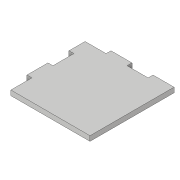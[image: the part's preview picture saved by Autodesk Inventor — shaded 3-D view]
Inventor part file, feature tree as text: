
AUTODESK INVENTOR PART (.ipt)
format: ipt  version: 2017 (Build 210142000, 142)  size: 99,840 bytes
history: native  units: in
note: dims shown in document units (in); Inventor stores cm internally (conversion verified against a paired STEP export)
features: extrude x2, sketch x2
ambient origin geometry x8: Origin, YZ Plane, XZ Plane, XY Plane, X Axis, Y Axis, Z Axis, Center Point
bodies: Solid1 (feature_tree)
feature tree (4):
  extrude  "Extrusion1"  Depth=2.0in
  extrude  "Extrusion2"  Depth=0.117in
  sketch  "Sketch1"  dims[d0=2.0in d1=2.0in]
  sketch  "Sketch2"  dims[d2=0.117in d3=0.0in d4=0.117in d5=0.5in d6=0.117in d7=0.5in d8=0.5in d9=0.117in d10=0.5in d11=0.117in d12=0.117in d13=0.0in]
